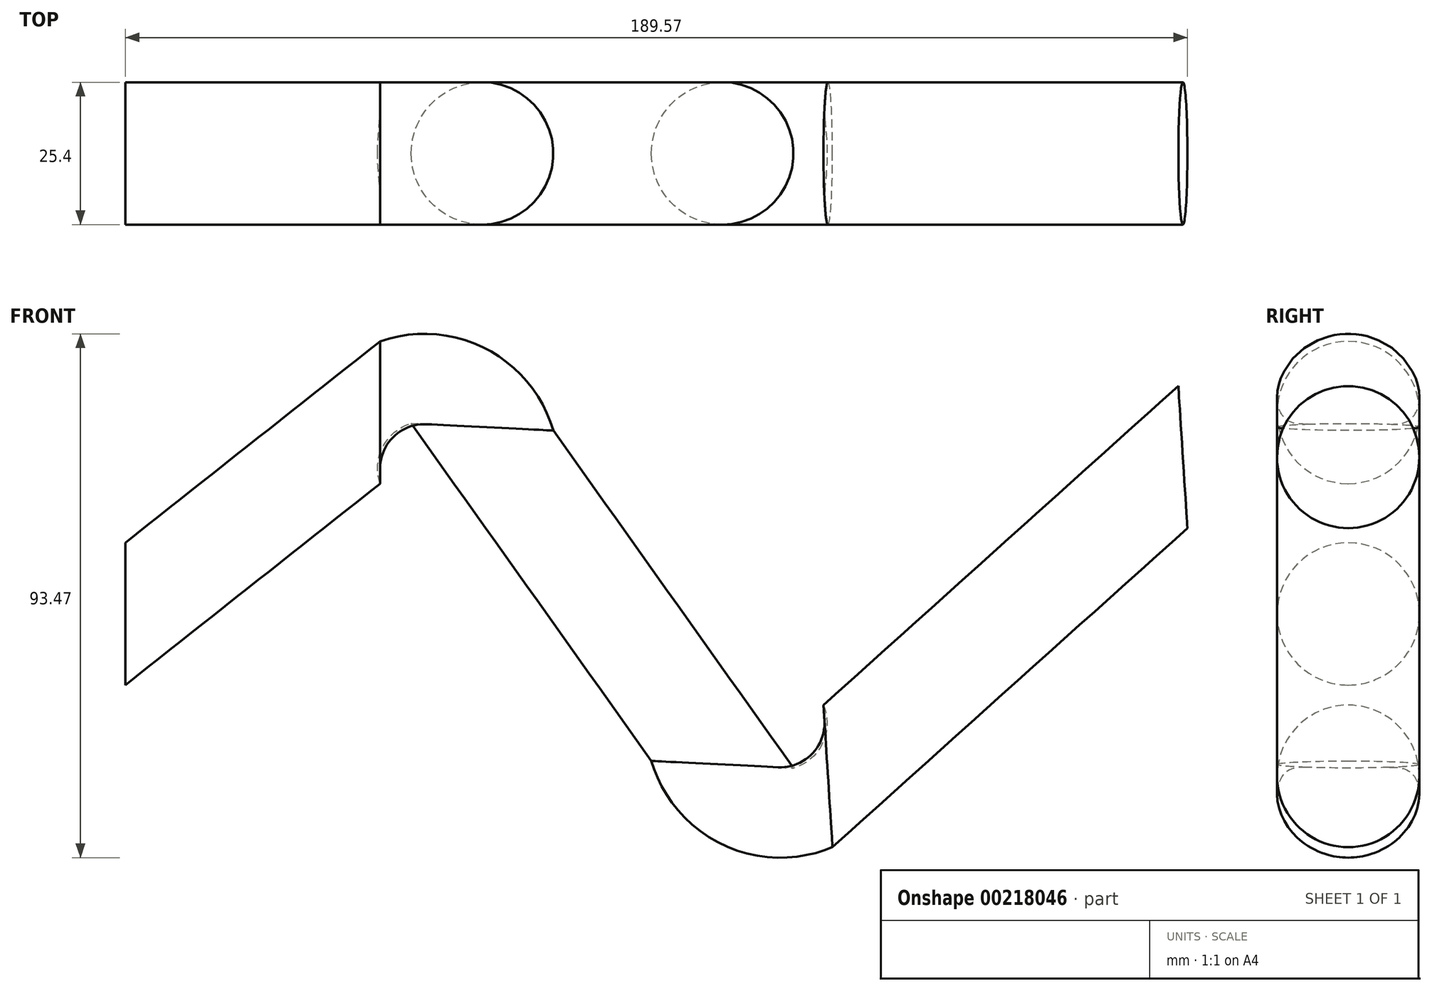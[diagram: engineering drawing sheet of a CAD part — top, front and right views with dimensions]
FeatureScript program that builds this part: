
annotation { "Feature Type Name" : "Feature", "Feature Type Description" : "" }
export const myFeature = defineFeature(function(context is Context, id is Id, definition is map)
    precondition{}
    {
        {
            var Q0;
            Q0=qCreatedBy(makeId("Right.planeOp"),FACE);
            var sketch = newSketch(context, id + "F0", { "sketchPlane" : qUnion([Q0])});
            skCircle(sketch, "E0", {"center": v(0, 0) * mm, "radius": 12.7 * mm});
            skSolve(sketch);
        }
        {
            var Q0;
            Q0=qCreatedBy(makeId("Front.planeOp"),FACE);
            var sketch = newSketch(context, id + "F1", { "sketchPlane" : qUnion([Q0])});
            skLineSegment(sketch, "E1", {"start": v(0, 0) * mm, "end": v(45.5, 35.94) * mm});
            skLineSegment(sketch, "E2", {"start": v(63.72, 33.34) * mm, "end": v(106.58, -26.87) * mm});
            skLineSegment(sketch, "E3", {"start": v(125.42, -28.95) * mm, "end": v(188.77, 27.97) * mm});
            skPoint(sketch, "E4.visualSharp", {"position": v(55.97, 44.22) * mm});
            skArc(sketch, "E4.filletArc", {"start": v(63.72, 33.34) * mm, "mid": v(55.17, 38.55) * mm, "end": v(45.5, 35.94) * mm});
            skPoint(sketch, "E5.visualSharp", {"position": v(114.84, -38.46) * mm});
            skArc(sketch, "E5.filletArc", {"start": v(106.58, -26.87) * mm, "mid": v(115.54, -32.13) * mm, "end": v(125.42, -28.95) * mm});
            skSolve(sketch);
        }
        {
            var Q0;
            Q0=makeQuery(id+"F0.imprint","IMPRINT",FACE,{"disambiguationData":[TD([[makeQuery(id+"F0.imprint","IMPRINT",EDGE,{"derivedFrom":sQuery(id+"F0.wireOp",EDGE,"E0")}),1.0]])]});
            var Q1;
            Q1 = qSketchRegion(id + "F1", true);
            var Q2;
            Q2=sQuery(id+"F1.wireOp",EDGE,"E1");
            var Q3;
            Q3=sQuery(id+"F1.wireOp",EDGE,"E4.filletArc");
            var Q4;
            Q4=sQuery(id+"F1.wireOp",EDGE,"E5.filletArc");
            var Q5;
            Q5=sQuery(id+"F1.wireOp",EDGE,"E2");
            var Q6;
            Q6=sQuery(id+"F1.wireOp",EDGE,"E3");
            sweep(context, id + "F2", {"profiles" : qUnion([Q0, Q1]), "path" : qUnion([Q2, Q3, Q4, Q5, Q6])});
        }
    });
